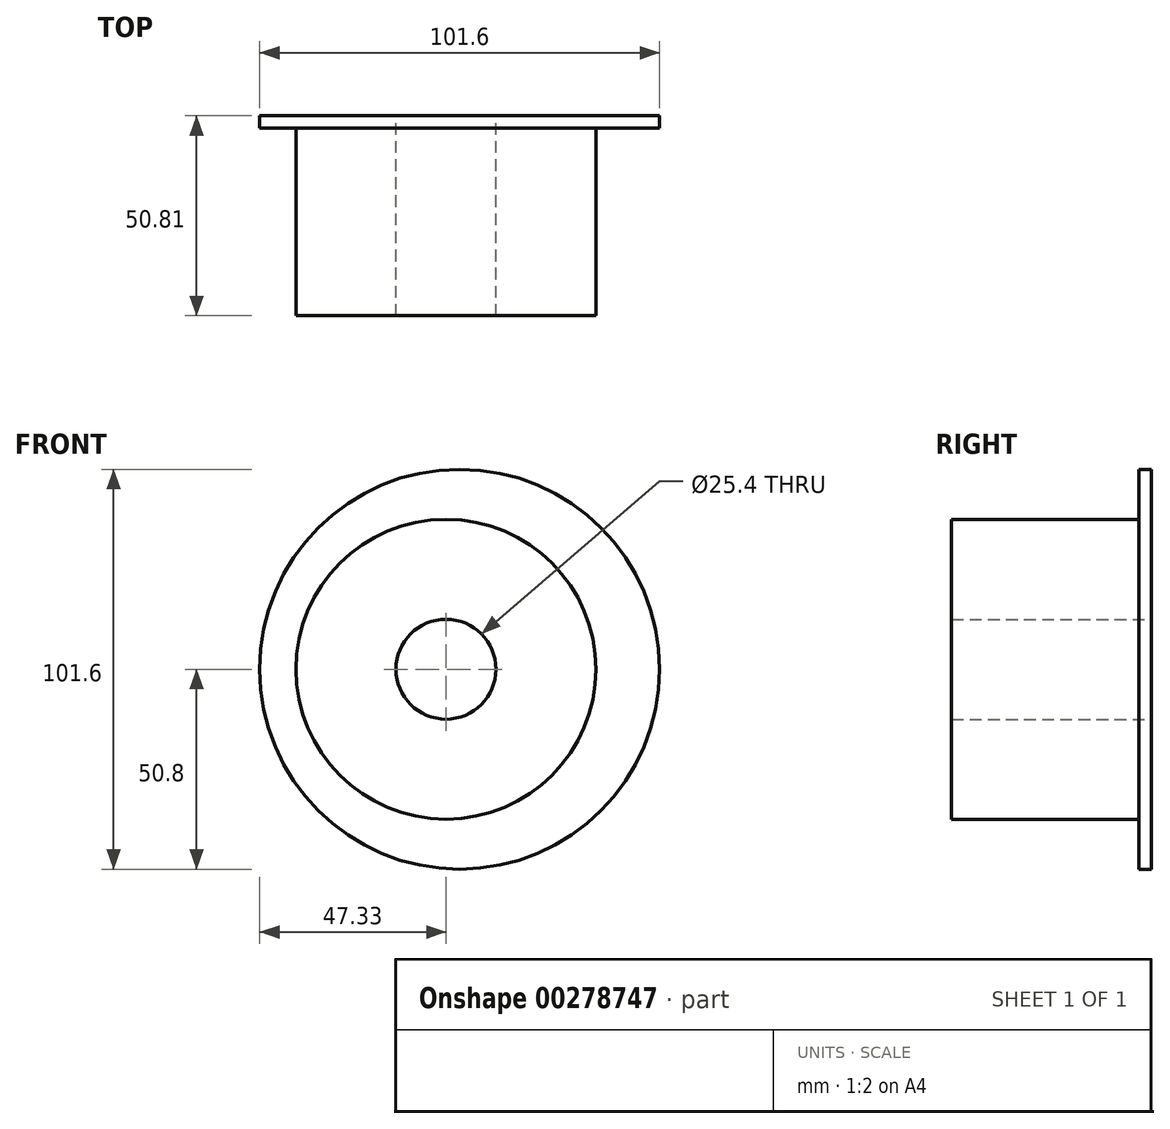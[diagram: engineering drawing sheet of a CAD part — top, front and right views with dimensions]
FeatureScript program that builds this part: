
annotation { "Feature Type Name" : "Feature", "Feature Type Description" : "" }
export const myFeature = defineFeature(function(context is Context, id is Id, definition is map)
    precondition{}
    {
        {
            var Q0;
            Q0=qCreatedBy(makeId("Front.planeOp"),FACE);
            var sketch = newSketch(context, id + "F0", { "sketchPlane" : qUnion([Q0])});
            skCircle(sketch, "E0", {"center": v(0, 0) * mm, "radius": 38.1 * mm});
            skSolve(sketch);
        }
        {
            var Q0;
            Q0=makeQuery(id+"F0.imprint","IMPRINT",FACE,{"disambiguationData":[TD([[makeQuery(id+"F0.imprint","IMPRINT",EDGE,{"derivedFrom":sQuery(id+"F0.wireOp",EDGE,"E0")}),1.0]])]});
            extrude(context, id + "F1", {"entities" : qUnion([Q0]), "depth" : 47.62 * mm});
        }
        {
            var Q0;
            Q0=qCreatedBy(makeId("Front.planeOp"),FACE);
            var sketch = newSketch(context, id + "F2", { "sketchPlane" : qUnion([Q0])});
            skCircle(sketch, "E1", {"center": v(3.47, 0) * mm, "radius": 50.8 * mm});
            skSolve(sketch);
        }
        {
            var Q0;
            Q0=makeQuery(id+"F2.imprint","IMPRINT",FACE,{"disambiguationData":[TD([[makeQuery(id+"F2.imprint","IMPRINT",EDGE,{"derivedFrom":sQuery(id+"F2.wireOp",EDGE,"E1")}),1.0]])]});
            extrude(context, id + "F3", {"entities" : qUnion([Q0]), "operationType" : NewBodyOperationType.ADD, "oppositeDirection" : true, "depth" : 3.17 * mm});
        }
        {
            var Q0;
            Q0=qCreatedBy(makeId("Front.planeOp"),FACE);
            var sketch = newSketch(context, id + "F4", { "sketchPlane" : qUnion([Q0])});
            skCircle(sketch, "E2", {"center": v(0, 0) * mm, "radius": 12.7 * mm});
            skSolve(sketch);
        }
        {
            var Q0;
            Q0 = qSketchRegion(id + "F4", true);
            var Q1;
            Q1=makeQuery(id+"F1.opExtrude","CAP_FACE",FACE,{"disambiguationData":[OSD([sQuery(id+"F0.wireOp",EDGE,"E0")])],"isStart":false});
            var Q2;
            Q2=makeQuery(id+"F1.opExtrude","CAP_FACE",FACE,{"disambiguationData":[OSD([sQuery(id+"F0.wireOp",EDGE,"E0")])],"isStart":false});
            extrude(context, id + "F5", {"entities" : qUnion([Q0]), "operationType" : NewBodyOperationType.REMOVE, "endBound" : BoundingType.UP_TO_SURFACE, "endBoundEntityFace" : qUnion([Q1]), "depth" : 25.4 * mm});
        }
        {
            var Q0;
            Q0 = qSketchRegion(id + "F4", true);
            var Q1;
            Q1=makeQuery(id+"F3.opExtrude","CAP_FACE",FACE,{"disambiguationData":[OSD([sQuery(id+"F2.wireOp",EDGE,"E1")])],"isStart":false});
            extrude(context, id + "F6", {"entities" : qUnion([Q0]), "operationType" : NewBodyOperationType.REMOVE, "endBound" : BoundingType.UP_TO_SURFACE, "oppositeDirection" : true, "endBoundEntityFace" : qUnion([Q1]), "depth" : 25.4 * mm});
        }
    });
